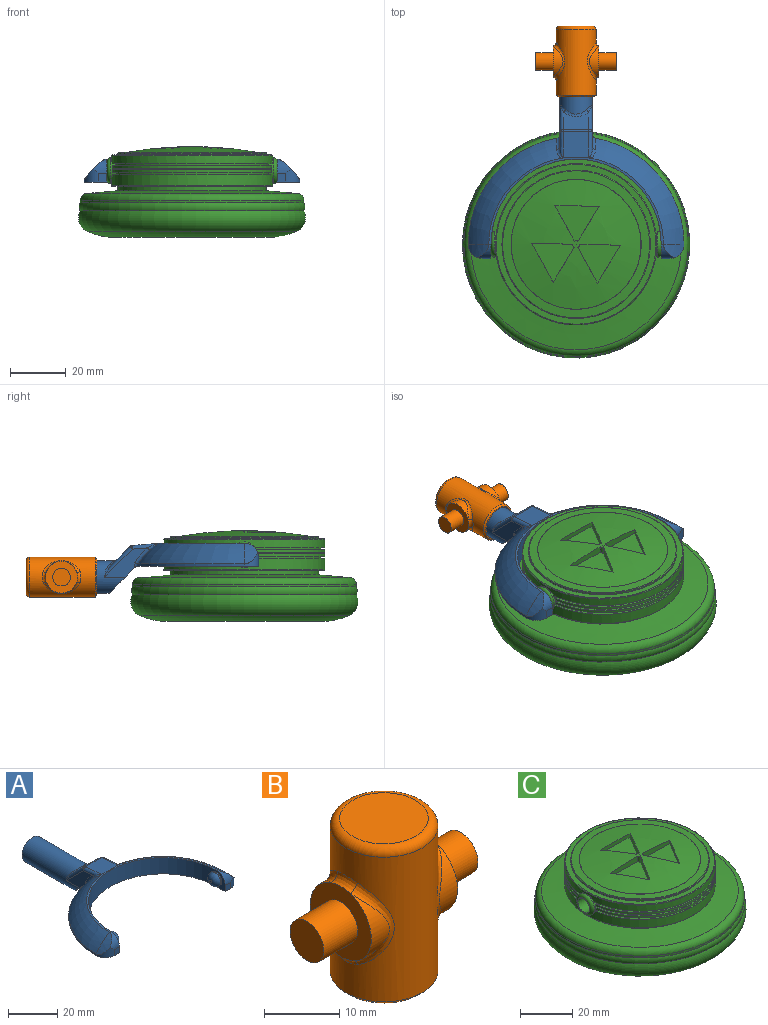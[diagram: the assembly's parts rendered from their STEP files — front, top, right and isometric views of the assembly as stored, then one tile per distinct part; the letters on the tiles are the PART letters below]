
ASSEMBLY  parts=3 mates=2
PART A: 48 faces, bbox 77.3x80.8x18.2 mm
  f0: plane 11.99x9.83mm, normal (0,-0.71,-0.71), area 141.5mm2, adj f1,f2,f9,f30,f43,f46
  f1: plane 15.39x10.49mm, normal (-1,0,0), area 63.5mm2, adj f0,f30,f32,f36,f46,f47
  f2: plane 15.39x10.49mm, normal (1,0,0), area 63.5mm2, adj f0,f30,f34,f39,f43,f44
  f3: plane 9.14x6.37mm, normal (0,0.71,0.71), area 67.6mm2, adj f35,f36,f39,f40
  f4: cylinder r=38.61mm len=37.99mm, axis (0,0,-1), area 42.6mm2, adj f6,f9,f17,f46,f47
  f5: torus R=19.3mm, axis (0,0,-1), area 507.8mm2, adj f10,f11,f12,f29,f42,f44
  f6: torus R=19.3mm, axis (0,0,-1), area 507.8mm2, adj f4,f11,f15,f28,f45,f47
  f7: cylinder r=30.48mm len=60.96mm, axis (0,0,-1), area 746.6mm2, adj f8,f9,f11,f14,f21,f24
  f8: plane 8.13x5.08mm, normal (-1,0,0), area 19.9mm2, adj f7,f9,f13,f19,f24
  f9: plane 77.22x43.73mm, normal (0,0,-1), area 956.2mm2, adj f0,f4,f7,f8,f10,f13,f14,f16
  f10: cylinder r=38.61mm len=37.99mm, axis (0,0,-1), area 42.6mm2, adj f5,f9,f20,f43,f44
  f11: plane 62.55x30.95mm, normal (0,0,1), area 75mm2, adj f5,f6,f7,f18,f19,f27
  f12: cylinder r=22.71mm len=7.33mm, axis (0,1,0), area 24.8mm2, adj f5,f19,f20
  f13: plane 3.05x3.05mm, normal (0,-1,0), area 9.3mm2, adj f8,f9,f19,f20
  f14: plane 8.13x5.08mm, normal (1,0,0), area 19.9mm2, adj f7,f9,f16,f18,f21
  f15: cylinder r=22.71mm len=7.33mm, axis (0,1,0), area 24.8mm2, adj f6,f17,f18
  f16: plane 3.05x3.05mm, normal (0,-1,0), area 9.3mm2, adj f9,f14,f17,f18
  f17: cylinder r=5.08mm len=5.08mm, axis (0,0,-1), area 21.9mm2, adj f4,f9,f15,f16,f18
  f18: cylinder r=5.08mm len=5.08mm, axis (-1,0,0), area 21.9mm2, adj f11,f14,f15,f16,f17
  f19: cylinder r=5.08mm len=5.08mm, axis (-1,0,0), area 21.9mm2, adj f8,f11,f12,f13,f20
  f20: cylinder r=5.08mm len=5.08mm, axis (0,0,-1), area 21.9mm2, adj f9,f10,f12,f13,f19
  f21: cylinder r=3.17mm len=6.35mm, axis (-1,0,0), area 12.7mm2, adj f7,f14,f23
  f22: plane 1.27x1.27mm, normal (1,0,0), area 1.3mm2, adj f23
  f23: torus R=0.64mm, axis (1,0,0), area 56.5mm2, adj f21,f22
  f24: cylinder r=3.17mm len=6.35mm, axis (1,0,0), area 12.7mm2, adj f7,f8,f26
  f25: plane 1.27x1.27mm, normal (-1,0,0), area 1.3mm2, adj f26
  f26: torus R=0.64mm, axis (-1,0,0), area 56.5mm2, adj f24,f25
  f27: plane 9.86x9.36mm, normal (0,0.09,1), area 85.6mm2, adj f11,f28,f29,f32,f34,f35,f42,f45
  f28: plane 1.04x0.17mm, normal (0,-1,0), area 0mm2, adj f6,f27,f45
  f29: plane 1.04x0.17mm, normal (0,-1,0), area 0mm2, adj f5,f27,f42
  f30: cylinder r=5.84mm len=33.01mm, axis (0,-1,0), area 1029.7mm2, adj f0,f1,f2,f31,f38,f40,f41
  f31: plane 11.68x11.68mm, normal (0,1,0), area 107.2mm2, adj f30
  f32: cylinder r=1.27mm len=9.13mm, axis (0,-1,0.09), area 14.4mm2, adj f1,f27,f33,f45
  f33: sphere r=1.27mm, area 1.5mm2, adj f32,f35,f36
  f34: cylinder r=1.27mm len=9.13mm, axis (0,1,-0.09), area 14.4mm2, adj f2,f27,f37,f42
  f35: cylinder r=1.27mm len=9.14mm, axis (-1,0,0), area 8.1mm2, adj f3,f27,f33,f37
  f36: cylinder r=1.27mm len=10.91mm, axis (0,-0.71,0.71), area 23.1mm2, adj f1,f3,f33,f38
  f37: sphere r=1.27mm, area 1.5mm2, adj f34,f35,f39
  f38: bspline ~4.55x2.75mm, area 2.3mm2, adj f30,f36,f40
  f39: cylinder r=1.27mm len=10.91mm, axis (0,0.71,-0.71), area 23.1mm2, adj f2,f3,f37,f41
  f40: bspline ~9.14x2.56mm, area 10.7mm2, adj f3,f30,f38,f41
  f41: bspline ~5.23x3.53mm, area 2.3mm2, adj f30,f39,f40
  f42: bspline ~4.62x3.14mm, area 5.2mm2, adj f5,f27,f29,f34,f44
  f43: cylinder r=1.27mm len=1.74mm, axis (0,0,-1), area 1.9mm2, adj f0,f2,f9,f10,f44
  f44: bspline ~8.6x7.86mm, area 11.9mm2, adj f2,f5,f10,f42,f43
  f45: bspline ~4.62x3.14mm, area 5.2mm2, adj f6,f27,f28,f32,f47
  f46: cylinder r=1.27mm len=1.74mm, axis (0,0,-1), area 1.9mm2, adj f0,f1,f4,f9,f47
  f47: bspline ~8.6x7.86mm, area 11.9mm2, adj f1,f4,f6,f45,f46
PART B: 25 faces, bbox 28.9x15.5x25.4 mm
  f0: cylinder r=5.71mm len=10.81mm, axis (-1,0,0), area 26.2mm2, adj f5,f15
  f1: cylinder r=5.71mm len=10.81mm, axis (-1,0,0), area 26.2mm2, adj f8,f11
  f2: cylinder r=7.14mm len=23.5mm, axis (0,0,-1), area 763.2mm2, adj f9,f10,f11,f12,f13,f14,f15,f16
  f3: plane 11.75x11.75mm, normal (0,0,1), area 108.4mm2, adj f17
  f4: plane 13.02x13.02mm, normal (0,0,-1), area 16.3mm2, adj f22,f24
  f5: plane 11.46x11.46mm, normal (1,0,0), area 70.9mm2, adj f0,f6,f13,f16,f18
  f6: cylinder r=5.71mm len=10.81mm, axis (-1,0,0), area 26.2mm2, adj f5,f14
  f7: cylinder r=5.71mm len=10.81mm, axis (-1,0,0), area 26.2mm2, adj f8,f10
  f8: plane 11.46x11.46mm, normal (-1,0,0), area 70.9mm2, adj f1,f7,f9,f12,f20
  f9: bspline ~4.64x1.73mm, area 6.5mm2, adj f2,f8,f10,f11
  f10: bspline ~13.62x4.91mm, area 20.7mm2, adj f2,f7,f9,f12
  f11: bspline ~13.6x4.87mm, area 20.7mm2, adj f1,f2,f9,f12
  f12: bspline ~4.64x1.73mm, area 6.5mm2, adj f2,f8,f10,f11
  f13: bspline ~4.64x1.73mm, area 6.5mm2, adj f2,f5,f14,f15
  f14: bspline ~13.62x4.91mm, area 20.7mm2, adj f2,f6,f13,f16
  f15: bspline ~13.6x4.87mm, area 20.7mm2, adj f0,f2,f13,f16
  f16: bspline ~4.64x1.73mm, area 6.5mm2, adj f2,f5,f14,f15
  f17: torus R=5.87mm, axis (0,0,1), area 83.8mm2, adj f2,f3
  f18: cylinder r=3.17mm len=6.35mm, axis (-1,0,0), area 126.7mm2, adj f5,f19
  f19: plane 6.35x6.35mm, normal (1,0,0), area 31.7mm2, adj f18
  f20: cylinder r=3.17mm len=6.35mm, axis (1,0,0), area 126.7mm2, adj f8,f21
  f21: plane 6.35x6.35mm, normal (-1,0,0), area 31.7mm2, adj f20
  f22: cylinder r=6.1mm len=22.86mm, axis (0,0,-1), area 875.6mm2, adj f4,f23
  f23: plane 12.19x12.19mm, normal (0,0,-1), area 116.7mm2, adj f22
  f24: cone r=7.14mm half-angle=45deg, axis (0,0,1), area 38.5mm2, adj f2,f4
PART C: 64 faces, bbox 96.2x96.2x32.5 mm
  f0: cylinder r=28.87mm len=57.73mm, axis (0,0,-1), area 688.1mm2, adj f1,f2,f54,f55,f60
  f1: plane 57.07x24.5mm, normal (0,0,1), area 101.5mm2, adj f0,f3,f54,f55
  f2: plane 57.07x24.5mm, normal (0,0,1), area 101.5mm2, adj f0,f4,f54,f55
  f3: cylinder r=27.6mm len=54.5mm, axis (0,0,-1), area 49.4mm2, adj f1,f6,f54,f55
  f4: cylinder r=27.6mm len=54.5mm, axis (0,0,-1), area 49.4mm2, adj f2,f5,f54,f55
  f5: plane 57.02x24.35mm, normal (0,0,-1), area 101.1mm2, adj f4,f8,f54,f55
  f6: plane 57.02x24.35mm, normal (0,0,-1), area 101.1mm2, adj f3,f7,f54,f55
  f7: cylinder r=28.87mm len=57.02mm, axis (0,0,-1), area 77.7mm2, adj f6,f9,f54,f55
  f8: cylinder r=28.87mm len=57.02mm, axis (0,0,-1), area 77.7mm2, adj f5,f10,f54,f55
  f9: plane 57.01x24.3mm, normal (0,0,1), area 101mm2, adj f7,f11,f54,f55
  f10: plane 57.01x24.3mm, normal (0,0,1), area 101mm2, adj f8,f12,f54,f55
  f11: cylinder r=27.6mm len=54.46mm, axis (0,0,-1), area 49.3mm2, adj f9,f13,f54,f55
  f12: cylinder r=27.6mm len=54.46mm, axis (0,0,-1), area 49.3mm2, adj f10,f14,f54,f55
  f13: plane 57.03x24.38mm, normal (0,0,-1), area 101.2mm2, adj f11,f15,f54,f55
  f14: plane 57.03x24.38mm, normal (0,0,-1), area 101.2mm2, adj f12,f16,f54,f55
  f15: cylinder r=28.87mm len=57.12mm, axis (0,0,-1), area 78.1mm2, adj f13,f22,f54,f55
  f16: cylinder r=28.87mm len=57.12mm, axis (0,0,-1), area 78.1mm2, adj f14,f21,f54,f55
  f17: cylinder r=27.6mm len=54.66mm, axis (0,0,-1), area 49.9mm2, adj f19,f22,f54,f55
  f18: cylinder r=27.6mm len=54.66mm, axis (0,0,-1), area 49.9mm2, adj f20,f21,f54,f55
  f19: plane 57.22x25.02mm, normal (0,0,-1), area 102.8mm2, adj f17,f23,f54,f55
  f20: plane 57.22x25.02mm, normal (0,0,-1), area 102.8mm2, adj f18,f23,f54,f55
  f21: plane 57.12x24.68mm, normal (0,0,1), area 102mm2, adj f16,f18,f54,f55
  f22: plane 57.12x24.68mm, normal (0,0,1), area 102mm2, adj f15,f17,f54,f55
  f23: cylinder r=28.87mm len=57.73mm, axis (0,0,-1), area 502.8mm2, adj f19,f20,f54,f55,f61
  f24: sphere r=135.39mm, area 1385.3mm2, adj f38,f39,f40,f41,f43,f44,f45,f46
  f25: plane 39.33x39.33mm, normal (0,0,-1), area 1214.6mm2, adj f26
  f26: torus R=20.12mm, axis (0,0,-1), area 1429.3mm2, adj f25,f27
  f27: torus R=27.74mm, axis (0,0,-1), area 3542.1mm2, adj f26,f28
  f28: torus R=35.36mm, axis (0,0,-1), area 2180.1mm2, adj f27,f29
  f29: torus R=37.35mm, axis (0,0,-1), area 734.6mm2, adj f28,f30
  f30: cylinder r=40.06mm len=80.11mm, axis (0,0,-1), area 213.3mm2, adj f29,f34
  f31: cone r=26.57mm half-angle=85deg, axis (0,0,-1), area 2265mm2, adj f32,f34
  f32: cylinder r=26.57mm len=53.14mm, axis (0,0,-1), area 265mm2, adj f31,f33
  f33: plane 57.23x57.23mm, normal (0,0,-1), area 354.5mm2, adj f32,f60
  f34: torus R=37.52mm, axis (0,0,1), area 928.6mm2, adj f30,f31
  f35: cone r=26.57mm half-angle=87deg, axis (0,0,-1), area 475.4mm2, adj f62,f63
  f36: cylinder r=26.57mm len=53.14mm, axis (0,0,-1), area 92.3mm2, adj f37,f62
  f37: plane 57.23x57.23mm, normal (0,0,1), area 354.5mm2, adj f36,f61
  f38: cylinder r=1.27mm len=2.53mm, axis (0,0,1), area 3.4mm2, adj f24,f39,f41,f42
  f39: plane 12.8x7.04mm, normal (0.88,0.48,0), area 32.2mm2, adj f24,f38,f40,f42
  f40: plane 13.58x8.22mm, normal (-0.86,0.52,0), area 28mm2, adj f24,f39,f41,f42
  f41: plane 14.6x2.53mm, normal (-0.02,-1,0), area 32.2mm2, adj f24,f38,f40,f42
  f42: plane 15.26x13.88mm, normal (0,0,1), area 108.3mm2, adj f38,f39,f40,f41
  f43: plane 12.49x7.56mm, normal (-0.86,0.52,0), area 32.2mm2, adj f24,f44,f46,f47
  f44: cylinder r=1.27mm len=2.53mm, axis (0,0,1), area 3.4mm2, adj f24,f43,f45,f47
  f45: plane 14.6x2.53mm, normal (-0.02,-1,0), area 32.2mm2, adj f24,f44,f46,f47
  f46: plane 13.91x7.65mm, normal (0.88,0.48,0), area 28mm2, adj f24,f43,f45,f47
  f47: plane 15.21x13.91mm, normal (0,0,1), area 108.3mm2, adj f43,f44,f45,f46
  f48: cylinder r=1.27mm len=2.53mm, axis (0,0,1), area 3.4mm2, adj f24,f49,f51,f52
  f49: plane 12.49x7.56mm, normal (-0.86,0.52,0), area 32.2mm2, adj f24,f48,f50,f52
  f50: plane 15.87x1.84mm, normal (-0.02,-1,0), area 28mm2, adj f24,f49,f51,f52
  f51: plane 12.8x7.04mm, normal (0.88,0.48,0), area 32.2mm2, adj f24,f48,f50,f52
  f52: plane 15.87x12.82mm, normal (0,0,1), area 108.3mm2, adj f48,f49,f50,f51
  f53: plane 6.6x6.6mm, normal (1,0,0), area 2.6mm2, adj f58,f59
  f54: cylinder r=4.57mm len=9.14mm, axis (-1,0,0), area 20.2mm2, adj f0,f1,f2,f3,f4,f5,f6,f7
  f55: cylinder r=4.57mm len=9.14mm, axis (-1,0,0), area 20.2mm2, adj f0,f1,f2,f3,f4,f5,f6,f7
  f56: plane 6.6x6.6mm, normal (-1,0,0), area 2.6mm2, adj f57,f59
  f57: torus R=3.3mm, axis (1,0,0), area 51.5mm2, adj f55,f56
  f58: torus R=3.3mm, axis (1,0,0), area 51.5mm2, adj f53,f54
  f59: cylinder r=3.17mm len=60.96mm, axis (1,0,0), area 1216.1mm2, adj f53,f56
  f60: torus R=28.61mm, axis (0,0,1), area 72.1mm2, adj f0,f33
  f61: torus R=28.61mm, axis (0,0,-1), area 72.1mm2, adj f23,f37
  f62: torus R=26.31mm, axis (0,0,1), area 64.2mm2, adj f35,f36
  f63: torus R=23.29mm, axis (0,0,1), area 4.5mm2, adj f24,f35
PLACE A t=(32.34,27.52,20.85)mm
PLACE B rot(axis=(-1,0,0),90deg) t=(32.34,80.3,16.88)mm
PLACE C t=(32.34,27.52,33.52)mm
MATE revolute A.f24 <-> C.f54  axis (-1,0,0) through (62.82,27.52,24.92)mm
MATE revolute B.f2 <-> A.f30  axis (0,-1,0) through (32.34,103.16,16.88)mm
